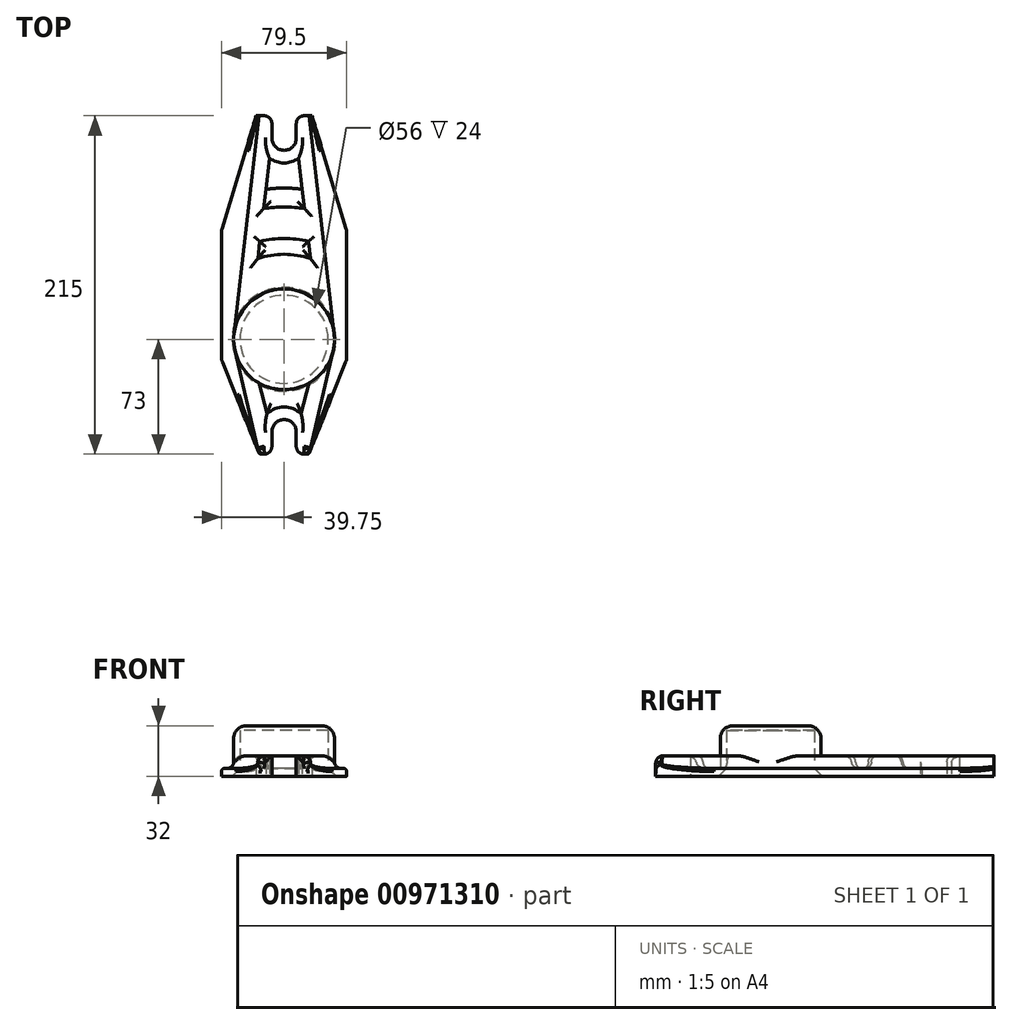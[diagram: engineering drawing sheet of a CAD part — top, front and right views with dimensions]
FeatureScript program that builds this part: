
annotation { "Feature Type Name" : "Feature", "Feature Type Description" : "" }
export const myFeature = defineFeature(function(context is Context, id is Id, definition is map)
    precondition{}
    {
        {
            var Q0;
            Q0=qCreatedBy(makeId("Top.planeOp"),FACE);
            var sketch = newSketch(context, id + "F0", { "sketchPlane" : qUnion([Q0])});
            skCircle(sketch, "E0", {"center": v(0, 0) * mm, "radius": 32 * mm});
            skLineSegment(sketch, "E1.bottom", {"start": v(-17.75, 142) * mm, "end": v(-7.75, 142) * mm});
            skLineSegment(sketch, "E1.top", {"start": v(-15.75, -73) * mm, "end": v(-7.75, -73) * mm});
            skLineSegment(sketch, "E1.left", {"start": v(-39.75, 69) * mm, "end": v(-39.75, -13) * mm});
            skLineSegment(sketch, "E1.right", {"start": v(39.75, 69) * mm, "end": v(39.75, -13) * mm});
            skLineSegment(sketch, "E2", {"start": v(0, 91.94) * mm, "end": v(0, -69.03) * mm, "construction": true});
            skLineSegment(sketch, "E3", {"start": v(-17.75, 142) * mm, "end": v(-39.75, 69) * mm});
            skLineSegment(sketch, "E4", {"start": v(-15.75, -73) * mm, "end": v(-39.75, -13) * mm});
            skArc(sketch, "E5", {"start": v(-7.75, 127.75) * mm, "mid": v(0, 120) * mm, "end": v(7.75, 127.75) * mm});
            skArc(sketch, "E6", {"start": v(7.75, -58.75) * mm, "mid": v(0, -51) * mm, "end": v(-7.75, -58.75) * mm});
            skLineSegment(sketch, "E7.MirrorCS", {"start": v(17.75, 142) * mm, "end": v(39.75, 69) * mm});
            skLineSegment(sketch, "E8.MirrorCS", {"start": v(15.75, -73) * mm, "end": v(39.75, -13) * mm});
            skCircle(sketch, "E9", {"center": v(0, 0) * mm, "radius": 22.5 * mm});
            skLineSegment(sketch, "E10.left", {"start": v(-7.75, 142) * mm, "end": v(-7.75, 127.75) * mm});
            skLineSegment(sketch, "E10.right", {"start": v(7.75, 142) * mm, "end": v(7.75, 127.75) * mm});
            skLineSegment(sketch, "E11.left", {"start": v(-7.75, -58.75) * mm, "end": v(-7.75, -73) * mm});
            skLineSegment(sketch, "E11.right", {"start": v(7.75, -58.75) * mm, "end": v(7.75, -73) * mm});
            skLineSegment(sketch, "E12.0", {"start": v(15.75, 142) * mm, "end": v(15.75, 127.75) * mm});
            skArc(sketch, "E12.1", {"start": v(-15.75, 127.75) * mm, "mid": v(0, 112) * mm, "end": v(15.75, 127.75) * mm});
            skLineSegment(sketch, "E12.2", {"start": v(-15.75, 142) * mm, "end": v(-15.75, 127.75) * mm});
            skLineSegment(sketch, "E13.0", {"start": v(-15.75, -58.75) * mm, "end": v(-15.75, -73) * mm});
            skArc(sketch, "E13.1", {"start": v(15.75, -58.75) * mm, "mid": v(0, -43) * mm, "end": v(-15.75, -58.75) * mm});
            skLineSegment(sketch, "E13.2", {"start": v(15.75, -58.75) * mm, "end": v(15.75, -73) * mm});
            skLineSegment(sketch, "E14.trimOffspring", {"start": v(7.75, 142) * mm, "end": v(17.75, 142) * mm});
            skLineSegment(sketch, "E15.trimOffspring", {"start": v(7.75, -73) * mm, "end": v(15.75, -73) * mm});
            skCircle(sketch, "E16", {"center": v(0, 0) * mm, "radius": 28 * mm});
            skLineSegment(sketch, "E17", {"start": v(-31.79, 3.69) * mm, "end": v(-15.75, 142) * mm});
            skLineSegment(sketch, "E18", {"start": v(31.79, 3.69) * mm, "end": v(15.75, 142) * mm});
            skLineSegment(sketch, "E19", {"start": v(7.75, 127.75) * mm, "end": v(22.65, 0) * mm});
            skLineSegment(sketch, "E20", {"start": v(-7.75, 127.75) * mm, "end": v(-22.35, 2.6) * mm});
            skLineSegment(sketch, "E21", {"start": v(31.15, -7.3) * mm, "end": v(15.75, -73) * mm});
            skLineSegment(sketch, "E22", {"start": v(-31.15, -7.3) * mm, "end": v(-15.75, -73) * mm});
            skLineSegment(sketch, "E23", {"start": v(-21.75, -5.75) * mm, "end": v(-7.75, -58.75) * mm});
            skLineSegment(sketch, "E24", {"start": v(21.75, -5.75) * mm, "end": v(7.75, -58.75) * mm});
            skArc(sketch, "E25", {"start": v(-16.66, 51.37) * mm, "mid": v(0, 54) * mm, "end": v(16.66, 51.37) * mm});
            skArc(sketch, "E26", {"start": v(-15.4, 62.12) * mm, "mid": v(0, 64) * mm, "end": v(15.4, 62.12) * mm});
            skArc(sketch, "E27", {"start": v(-12.97, 83) * mm, "mid": v(0, 84) * mm, "end": v(12.97, 83) * mm});
            skArc(sketch, "E28", {"start": v(-11.53, 95.3) * mm, "mid": v(0, 96) * mm, "end": v(11.53, 95.3) * mm});
            skSolve(sketch);
        }
        {
            var Q0;
            Q0 = qSketchRegion(id + "F0", true);
            var Q1;
            {var subQ0=sQuery(id+"F0.wireOp",EDGE,"E19");var subQ1=sQuery(id+"F0.wireOp",EDGE,"E0");var subQ2=makeQuery(id+"F0.imprint","INTERSECT",VERTEX,{"derivedFrom":[subQ1,subQ0]});Q1=makeQuery(id+"F0.imprint","IMPRINT",FACE,{"disambiguationData":[TD([[makeQuery(id+"F0.imprint","IMPRINT",EDGE,{"disambiguationData":[TD([[subQ2,-1.0]])],"derivedFrom":subQ1}),-1.0]])]});}
            var Q2;
            {var subQ0=sQuery(id+"F0.wireOp",EDGE,"E23");var subQ1=sQuery(id+"F0.wireOp",EDGE,"E0");var subQ2=makeQuery(id+"F0.imprint","INTERSECT",VERTEX,{"derivedFrom":[subQ1,subQ0]});Q2=makeQuery(id+"F0.imprint","IMPRINT",FACE,{"disambiguationData":[TD([[makeQuery(id+"F0.imprint","IMPRINT",EDGE,{"disambiguationData":[TD([[subQ2,-1.0]])],"derivedFrom":subQ1}),-1.0]])]});}
            var Q3;
            {var subQ5=sQuery(id+"F0.wireOp",EDGE,"E26");Q3=makeQuery(id+"F0.imprint","IMPRINT",FACE,{"disambiguationData":[TD([[makeQuery(id+"F0.imprint","IMPRINT",EDGE,{"derivedFrom":subQ5}),1.0]])]});}
            var Q4;
            {var subQ0=sQuery(id+"F0.wireOp",EDGE,"E25");Q4=makeQuery(id+"F0.imprint","IMPRINT",FACE,{"disambiguationData":[TD([[makeQuery(id+"F0.imprint","IMPRINT",EDGE,{"derivedFrom":subQ0}),1.0]])]});}
            var Q5;
            {var subQ0=sQuery(id+"F0.wireOp",EDGE,"E27");Q5=makeQuery(id+"F0.imprint","IMPRINT",FACE,{"disambiguationData":[TD([[makeQuery(id+"F0.imprint","IMPRINT",EDGE,{"derivedFrom":subQ0}),1.0]])]});}
            var Q6;
            {var subQ5=sQuery(id+"F0.wireOp",EDGE,"E28");Q6=makeQuery(id+"F0.imprint","IMPRINT",FACE,{"disambiguationData":[TD([[makeQuery(id+"F0.imprint","IMPRINT",EDGE,{"derivedFrom":subQ5}),1.0]])]});}
            extrude(context, id + "F1", {"entities" : qUnion([Q0, Q1, Q2, Q3, Q4, Q5, Q6]), "depth" : 5 * mm, "offsetDistance" : 25 * mm});
        }
        {
            var Q0;
            Q0=makeQuery(id+"F0.imprint","IMPRINT",FACE,{"disambiguationData":[TD([[makeQuery(id+"F0.imprint","IMPRINT",EDGE,{"derivedFrom":sQuery(id+"F0.wireOp",EDGE,"E6")}),-1.0]])]});
            var Q1;
            Q1=makeQuery(id+"F0.imprint","IMPRINT",FACE,{"disambiguationData":[TD([[makeQuery(id+"F0.imprint","IMPRINT",EDGE,{"derivedFrom":sQuery(id+"F0.wireOp",EDGE,"E5")}),-1.0]])]});
            var Q2;
            {var subQ1=sQuery(id+"F0.wireOp",EDGE,"E10.right");Q2=makeQuery(id+"F0.imprint","IMPRINT",FACE,{"disambiguationData":[TD([[makeQuery(id+"F0.imprint","IMPRINT",EDGE,{"derivedFrom":subQ1}),1.0]])]});}
            var Q3;
            {var subQ4=sQuery(id+"F0.wireOp",EDGE,"E10.left");Q3=makeQuery(id+"F0.imprint","IMPRINT",FACE,{"disambiguationData":[TD([[makeQuery(id+"F0.imprint","IMPRINT",EDGE,{"derivedFrom":subQ4}),-1.0]])]});}
            var Q4;
            Q4=makeQuery(id+"F0.imprint","IMPRINT",FACE,{"disambiguationData":[TD([[makeQuery(id+"F0.imprint","IMPRINT",EDGE,{"derivedFrom":sQuery(id+"F0.wireOp",EDGE,"E1.top")}),1.0]])]});
            var Q5;
            {var subQ4=sQuery(id+"F0.wireOp",EDGE,"E11.right");Q5=makeQuery(id+"F0.imprint","IMPRINT",FACE,{"disambiguationData":[TD([[makeQuery(id+"F0.imprint","IMPRINT",EDGE,{"derivedFrom":subQ4}),1.0]])]});}
            extrude(context, id + "F2", {"entities" : qUnion([Q0, Q1, Q2, Q3, Q4, Q5]), "operationType" : NewBodyOperationType.ADD, "depth" : 13 * mm, "offsetDistance" : 25 * mm});
        }
        {
            var Q0;
            Q0=makeQuery(id+"F0.imprint","IMPRINT",FACE,{"disambiguationData":[TD([[makeQuery(id+"F0.imprint","IMPRINT",EDGE,{"derivedFrom":sQuery(id+"F0.wireOp",EDGE,"E0")}),1.0]])]});
            var Q1;
            {var subQ0=sQuery(id+"F0.wireOp",EDGE,"E19");var subQ1=sQuery(id+"F0.wireOp",EDGE,"E0");var subQ2=makeQuery(id+"F0.imprint","INTERSECT",VERTEX,{"derivedFrom":[subQ1,subQ0]});Q1=makeQuery(id+"F0.imprint","IMPRINT",FACE,{"disambiguationData":[TD([[makeQuery(id+"F0.imprint","IMPRINT",EDGE,{"disambiguationData":[TD([[subQ2,-1.0]])],"derivedFrom":subQ1}),1.0]])]});}
            var Q2;
            {var subQ0=sQuery(id+"F0.wireOp",EDGE,"E23");var subQ1=sQuery(id+"F0.wireOp",EDGE,"E0");var subQ2=makeQuery(id+"F0.imprint","INTERSECT",VERTEX,{"derivedFrom":[subQ1,subQ0]});Q2=makeQuery(id+"F0.imprint","IMPRINT",FACE,{"disambiguationData":[TD([[makeQuery(id+"F0.imprint","IMPRINT",EDGE,{"disambiguationData":[TD([[subQ2,-1.0]])],"derivedFrom":subQ1}),1.0]])]});}
            extrude(context, id + "F3", {"entities" : qUnion([Q0, Q1, Q2]), "operationType" : NewBodyOperationType.ADD, "depth" : 29 * mm, "offsetDistance" : 25 * mm});
        }
        {
            var Q0;
            Q0=makeQuery(id+"F0.imprint","IMPRINT",FACE,{"disambiguationData":[TD([[makeQuery(id+"F0.imprint","IMPRINT",EDGE,{"derivedFrom":sQuery(id+"F0.wireOp",EDGE,"E0")}),1.0]])]});
            var Q1;
            Q1=makeQuery(id+"F0.imprint","IMPRINT",FACE,{"disambiguationData":[TD([[makeQuery(id+"F0.imprint","IMPRINT",EDGE,{"derivedFrom":sQuery(id+"F0.wireOp",EDGE,"E9")}),-1.0]])]});
            var Q2;
            Q2=makeQuery(id+"F0.imprint","IMPRINT",FACE,{"disambiguationData":[TD([[makeQuery(id+"F0.imprint","IMPRINT",EDGE,{"derivedFrom":sQuery(id+"F0.wireOp",EDGE,"E9")}),1.0]])]});
            var Q3;
            {var subQ0=sQuery(id+"F0.wireOp",EDGE,"E19");var subQ1=sQuery(id+"F0.wireOp",EDGE,"E0");var subQ2=makeQuery(id+"F0.imprint","INTERSECT",VERTEX,{"derivedFrom":[subQ1,subQ0]});Q3=makeQuery(id+"F0.imprint","IMPRINT",FACE,{"disambiguationData":[TD([[makeQuery(id+"F0.imprint","IMPRINT",EDGE,{"disambiguationData":[TD([[subQ2,-1.0]])],"derivedFrom":subQ1}),1.0]])]});}
            var Q4;
            {var subQ0=sQuery(id+"F0.wireOp",EDGE,"E23");var subQ1=sQuery(id+"F0.wireOp",EDGE,"E0");var subQ2=makeQuery(id+"F0.imprint","INTERSECT",VERTEX,{"derivedFrom":[subQ1,subQ0]});Q4=makeQuery(id+"F0.imprint","IMPRINT",FACE,{"disambiguationData":[TD([[makeQuery(id+"F0.imprint","IMPRINT",EDGE,{"disambiguationData":[TD([[subQ2,-1.0]])],"derivedFrom":subQ1}),1.0]])]});}
            extrude(context, id + "F4", {"entities" : qUnion([Q0, Q1, Q2, Q3, Q4]), "operationType" : NewBodyOperationType.ADD, "depth" : 32 * mm, "offsetDistance" : 25 * mm, "hasSecondDirection" : true, "secondDirectionOppositeDirection" : false, "secondDirectionDepth" : 29 * mm});
        }
        {
            var Q0;
            {var subQ1=sQuery(id+"F0.wireOp",EDGE,"E12.0");Q0=makeQuery(id+"F0.imprint","IMPRINT",FACE,{"disambiguationData":[TD([[makeQuery(id+"F0.imprint","IMPRINT",EDGE,{"derivedFrom":subQ1}),1.0]])]});}
            var Q1;
            {var subQ1=sQuery(id+"F0.wireOp",EDGE,"E12.2");Q1=makeQuery(id+"F0.imprint","IMPRINT",FACE,{"disambiguationData":[TD([[makeQuery(id+"F0.imprint","IMPRINT",EDGE,{"derivedFrom":subQ1}),-1.0]])]});}
            var Q2;
            {var subQ2=sQuery(id+"F0.wireOp",EDGE,"E13.0");Q2=makeQuery(id+"F0.imprint","IMPRINT",FACE,{"disambiguationData":[TD([[makeQuery(id+"F0.imprint","IMPRINT",EDGE,{"derivedFrom":subQ2}),-1.0]])]});}
            var Q3;
            {var subQ1=sQuery(id+"F0.wireOp",EDGE,"E13.2");Q3=makeQuery(id+"F0.imprint","IMPRINT",FACE,{"disambiguationData":[TD([[makeQuery(id+"F0.imprint","IMPRINT",EDGE,{"derivedFrom":subQ1}),1.0]])]});}
            var Q4;
            {var subQ0=sQuery(id+"F0.wireOp",EDGE,"E25");Q4=makeQuery(id+"F0.imprint","IMPRINT",FACE,{"disambiguationData":[TD([[makeQuery(id+"F0.imprint","IMPRINT",EDGE,{"derivedFrom":subQ0}),1.0]])]});}
            var Q5;
            {var subQ0=sQuery(id+"F0.wireOp",EDGE,"E27");Q5=makeQuery(id+"F0.imprint","IMPRINT",FACE,{"disambiguationData":[TD([[makeQuery(id+"F0.imprint","IMPRINT",EDGE,{"derivedFrom":subQ0}),1.0]])]});}
            extrude(context, id + "F5", {"entities" : qUnion([Q0, Q1, Q2, Q3, Q4, Q5]), "operationType" : NewBodyOperationType.ADD, "depth" : 13 * mm, "offsetDistance" : 25 * mm});
        }
        {
            var Q0;
            Q0=makeQuery(id+"F4.opExtrude","CAP_EDGE",EDGE,{"disambiguationData":[OSD([sQuery(id+"F0.wireOp",EDGE,"E0")])],"isStart":false});
            var Q1;
            Q1=makeQuery(id+"F1.opExtrude","SWEPT_EDGE",EDGE,{"disambiguationData":[OSD([sQuery(id+"F0.wireOp",EDGE,"E1.right"),sQuery(id+"F0.wireOp",EDGE,"E8.MirrorCS")])]});
            var Q2;
            Q2=makeQuery(id+"F1.opExtrude","SWEPT_EDGE",EDGE,{"disambiguationData":[OSD([sQuery(id+"F0.wireOp",EDGE,"E1.right"),sQuery(id+"F0.wireOp",EDGE,"E7.MirrorCS")])]});
            var Q3;
            Q3=makeQuery(id+"F1.opExtrude","SWEPT_EDGE",EDGE,{"disambiguationData":[OSD([sQuery(id+"F0.wireOp",EDGE,"E1.left"),sQuery(id+"F0.wireOp",EDGE,"E4")])]});
            var Q4;
            Q4=makeQuery(id+"F1.opExtrude","SWEPT_EDGE",EDGE,{"disambiguationData":[OSD([sQuery(id+"F0.wireOp",EDGE,"E1.left"),sQuery(id+"F0.wireOp",EDGE,"E3")])]});
            fillet(context, id + "F6", {"entities" : qUnion([Q0, Q1, Q2, Q3, Q4]), "radius" : 8 * mm, "allowEdgeOverflow" : false});
        }
        {
            var Q0;
            Q0=makeQuery(id+"F3.opExtrude","CAP_EDGE",EDGE,{"disambiguationData":[OSD([sQuery(id+"F0.wireOp",EDGE,"E16")])],"isStart":true});
            var Q1;
            Q1=makeQuery(id+"F3.opExtrude","CAP_EDGE",EDGE,{"disambiguationData":[OSD([sQuery(id+"F0.wireOp",EDGE,"E16")])],"isStart":false});
            chamfer(context, id + "F7", {"entities" : qUnion([Q0, Q1]), "width" : 5 * mm, "tangentPropagation" : true});
        }
        {
            var Q0;
            {var subQ0=sQuery(id+"F0.wireOp",EDGE,"E11.left");var subQ1=sQuery(id+"F0.wireOp",EDGE,"E1.top");Q0=makeQuery(id+"F2.boolean.opBoolean","MERGE",EDGE,{"derivedFrom":[makeQuery(id+"F1.opExtrude","SWEPT_EDGE",EDGE,{"disambiguationData":[OSD([subQ1,subQ0])]}),makeQuery(id+"F2.opExtrude","SWEPT_EDGE",EDGE,{"disambiguationData":[OSD([subQ1,subQ0])]})]});}
            var Q1;
            {var subQ0=sQuery(id+"F0.wireOp",EDGE,"E15.trimOffspring");var subQ1=sQuery(id+"F0.wireOp",EDGE,"E11.right");Q1=makeQuery(id+"F2.boolean.opBoolean","MERGE",EDGE,{"derivedFrom":[makeQuery(id+"F1.opExtrude","SWEPT_EDGE",EDGE,{"disambiguationData":[OSD([subQ1,subQ0])]}),makeQuery(id+"F2.opExtrude","SWEPT_EDGE",EDGE,{"disambiguationData":[OSD([subQ1,subQ0])]})]});}
            var Q2;
            {var subQ0=sQuery(id+"F0.wireOp",EDGE,"E10.left");var subQ1=sQuery(id+"F0.wireOp",EDGE,"E1.bottom");Q2=makeQuery(id+"F2.boolean.opBoolean","MERGE",EDGE,{"derivedFrom":[makeQuery(id+"F1.opExtrude","SWEPT_EDGE",EDGE,{"disambiguationData":[OSD([subQ1,subQ0])]}),makeQuery(id+"F2.opExtrude","SWEPT_EDGE",EDGE,{"disambiguationData":[OSD([subQ1,subQ0])]})]});}
            var Q3;
            {var subQ0=sQuery(id+"F0.wireOp",EDGE,"E14.trimOffspring");var subQ1=sQuery(id+"F0.wireOp",EDGE,"E10.right");Q3=makeQuery(id+"F2.boolean.opBoolean","MERGE",EDGE,{"derivedFrom":[makeQuery(id+"F1.opExtrude","SWEPT_EDGE",EDGE,{"disambiguationData":[OSD([subQ1,subQ0])]}),makeQuery(id+"F2.opExtrude","SWEPT_EDGE",EDGE,{"disambiguationData":[OSD([subQ1,subQ0])]})]});}
            fillet(context, id + "F8", {"entities" : qUnion([Q0, Q1, Q2, Q3]), "radius" : 5 * mm, "tangentPropagation" : true, "allowEdgeOverflow" : false});
        }
        {
            var Q0;
            Q0=makeQuery(id+"F5.boolean.opBoolean","INTERSECT",EDGE,{"derivedFrom":[makeQuery(id+"F1.opExtrude","CAP_FACE",FACE,{"disambiguationData":[OSD([sQuery(id+"F0.wireOp",EDGE,"E0"),sQuery(id+"F0.wireOp",EDGE,"E1.bottom"),sQuery(id+"F0.wireOp",EDGE,"E1.top"),sQuery(id+"F0.wireOp",EDGE,"E1.left"),sQuery(id+"F0.wireOp",EDGE,"E1.right"),sQuery(id+"F0.wireOp",EDGE,"E3"),sQuery(id+"F0.wireOp",EDGE,"E4"),sQuery(id+"F0.wireOp",EDGE,"E5"),sQuery(id+"F0.wireOp",EDGE,"E6"),sQuery(id+"F0.wireOp",EDGE,"E7.MirrorCS"),sQuery(id+"F0.wireOp",EDGE,"E8.MirrorCS"),sQuery(id+"F0.wireOp",EDGE,"E10.left"),sQuery(id+"F0.wireOp",EDGE,"E10.right"),sQuery(id+"F0.wireOp",EDGE,"E11.left"),sQuery(id+"F0.wireOp",EDGE,"E11.right"),sQuery(id+"F0.wireOp",EDGE,"E14.trimOffspring"),sQuery(id+"F0.wireOp",EDGE,"E15.trimOffspring")])],"isStart":false}),makeQuery(id+"F5.opExtrude","SWEPT_FACE",FACE,{"disambiguationData":[OSD([sQuery(id+"F0.wireOp",EDGE,"E20")])]})]});
            var Q1;
            {var subQ0=sQuery(id+"F0.wireOp",EDGE,"E0");Q1=makeQuery(id+"F5.boolean.opBoolean","SPLIT",EDGE,{"disambiguationData":[TD([makeQuery(id+"F5.opExtrude","SWEPT_FACE",FACE,{"disambiguationData":[OSD([sQuery(id+"F0.wireOp",EDGE,"E19")])]})])],"derivedFrom":makeQuery(id+"F1.opExtrude","CAP_EDGE",EDGE,{"disambiguationData":[OSD([subQ0])],"isStart":false})});}
            var Q2;
            Q2=makeQuery(id+"F5.opExtrude","CAP_EDGE",EDGE,{"disambiguationData":[OSD([sQuery(id+"F0.wireOp",EDGE,"E20")])],"isStart":false});
            var Q3;
            Q3=makeQuery(id+"F5.boolean.opBoolean","INTERSECT",EDGE,{"derivedFrom":[makeQuery(id+"F1.opExtrude","CAP_FACE",FACE,{"disambiguationData":[OSD([sQuery(id+"F0.wireOp",EDGE,"E0"),sQuery(id+"F0.wireOp",EDGE,"E1.bottom"),sQuery(id+"F0.wireOp",EDGE,"E1.top"),sQuery(id+"F0.wireOp",EDGE,"E1.left"),sQuery(id+"F0.wireOp",EDGE,"E1.right"),sQuery(id+"F0.wireOp",EDGE,"E3"),sQuery(id+"F0.wireOp",EDGE,"E4"),sQuery(id+"F0.wireOp",EDGE,"E5"),sQuery(id+"F0.wireOp",EDGE,"E6"),sQuery(id+"F0.wireOp",EDGE,"E7.MirrorCS"),sQuery(id+"F0.wireOp",EDGE,"E8.MirrorCS"),sQuery(id+"F0.wireOp",EDGE,"E10.left"),sQuery(id+"F0.wireOp",EDGE,"E10.right"),sQuery(id+"F0.wireOp",EDGE,"E11.left"),sQuery(id+"F0.wireOp",EDGE,"E11.right"),sQuery(id+"F0.wireOp",EDGE,"E14.trimOffspring"),sQuery(id+"F0.wireOp",EDGE,"E15.trimOffspring")])],"isStart":false}),makeQuery(id+"F5.opExtrude","SWEPT_FACE",FACE,{"disambiguationData":[OSD([sQuery(id+"F0.wireOp",EDGE,"E19")])]})]});
            var Q4;
            Q4=makeQuery(id+"F5.opExtrude","CAP_EDGE",EDGE,{"disambiguationData":[OSD([sQuery(id+"F0.wireOp",EDGE,"E19")])],"isStart":false});
            var Q5;
            Q5=makeQuery(id+"F2.boolean.opBoolean","INTERSECT",EDGE,{"derivedFrom":[makeQuery(id+"F1.opExtrude","CAP_FACE",FACE,{"disambiguationData":[OSD([sQuery(id+"F0.wireOp",EDGE,"E0"),sQuery(id+"F0.wireOp",EDGE,"E1.bottom"),sQuery(id+"F0.wireOp",EDGE,"E1.top"),sQuery(id+"F0.wireOp",EDGE,"E1.left"),sQuery(id+"F0.wireOp",EDGE,"E1.right"),sQuery(id+"F0.wireOp",EDGE,"E3"),sQuery(id+"F0.wireOp",EDGE,"E4"),sQuery(id+"F0.wireOp",EDGE,"E5"),sQuery(id+"F0.wireOp",EDGE,"E6"),sQuery(id+"F0.wireOp",EDGE,"E7.MirrorCS"),sQuery(id+"F0.wireOp",EDGE,"E8.MirrorCS"),sQuery(id+"F0.wireOp",EDGE,"E10.left"),sQuery(id+"F0.wireOp",EDGE,"E10.right"),sQuery(id+"F0.wireOp",EDGE,"E11.left"),sQuery(id+"F0.wireOp",EDGE,"E11.right"),sQuery(id+"F0.wireOp",EDGE,"E14.trimOffspring"),sQuery(id+"F0.wireOp",EDGE,"E15.trimOffspring")])],"isStart":false}),makeQuery(id+"F2.opExtrude","SWEPT_FACE",FACE,{"disambiguationData":[OSD([sQuery(id+"F0.wireOp",EDGE,"E12.1")])]})]});
            var Q6;
            Q6=makeQuery(id+"F2.opExtrude","CAP_EDGE",EDGE,{"disambiguationData":[OSD([sQuery(id+"F0.wireOp",EDGE,"E12.1")])],"isStart":false});
            var Q7;
            Q7=makeQuery(id+"F5.opExtrude","CAP_EDGE",EDGE,{"disambiguationData":[OSD([sQuery(id+"F0.wireOp",EDGE,"E18")])],"isStart":false});
            var Q8;
            Q8=makeQuery(id+"F5.opExtrude","CAP_EDGE",EDGE,{"disambiguationData":[OSD([sQuery(id+"F0.wireOp",EDGE,"E17")])],"isStart":false});
            var Q9;
            Q9=makeQuery(id+"F5.opExtrude","CAP_EDGE",EDGE,{"disambiguationData":[OSD([sQuery(id+"F0.wireOp",EDGE,"E22")])],"isStart":false});
            var Q10;
            {var subQ0=sQuery(id+"F0.wireOp",EDGE,"E0");Q10=makeQuery(id+"F5.boolean.opBoolean","SPLIT",EDGE,{"disambiguationData":[TD([makeQuery(id+"F5.opExtrude","SWEPT_FACE",FACE,{"disambiguationData":[OSD([sQuery(id+"F0.wireOp",EDGE,"E23")])]})])],"derivedFrom":makeQuery(id+"F1.opExtrude","CAP_EDGE",EDGE,{"disambiguationData":[OSD([subQ0])],"isStart":false})});}
            var Q11;
            Q11=makeQuery(id+"F5.opExtrude","CAP_EDGE",EDGE,{"disambiguationData":[OSD([sQuery(id+"F0.wireOp",EDGE,"E23")])],"isStart":false});
            var Q12;
            Q12=makeQuery(id+"F5.opExtrude","CAP_EDGE",EDGE,{"disambiguationData":[OSD([sQuery(id+"F0.wireOp",EDGE,"E24")])],"isStart":false});
            var Q13;
            Q13=makeQuery(id+"F2.opExtrude","CAP_EDGE",EDGE,{"disambiguationData":[OSD([sQuery(id+"F0.wireOp",EDGE,"E13.1")])],"isStart":false});
            var Q14;
            Q14=makeQuery(id+"F5.boolean.opBoolean","INTERSECT",EDGE,{"derivedFrom":[makeQuery(id+"F1.opExtrude","CAP_FACE",FACE,{"disambiguationData":[OSD([sQuery(id+"F0.wireOp",EDGE,"E0"),sQuery(id+"F0.wireOp",EDGE,"E1.bottom"),sQuery(id+"F0.wireOp",EDGE,"E1.top"),sQuery(id+"F0.wireOp",EDGE,"E1.left"),sQuery(id+"F0.wireOp",EDGE,"E1.right"),sQuery(id+"F0.wireOp",EDGE,"E3"),sQuery(id+"F0.wireOp",EDGE,"E4"),sQuery(id+"F0.wireOp",EDGE,"E5"),sQuery(id+"F0.wireOp",EDGE,"E6"),sQuery(id+"F0.wireOp",EDGE,"E7.MirrorCS"),sQuery(id+"F0.wireOp",EDGE,"E8.MirrorCS"),sQuery(id+"F0.wireOp",EDGE,"E10.left"),sQuery(id+"F0.wireOp",EDGE,"E10.right"),sQuery(id+"F0.wireOp",EDGE,"E11.left"),sQuery(id+"F0.wireOp",EDGE,"E11.right"),sQuery(id+"F0.wireOp",EDGE,"E14.trimOffspring"),sQuery(id+"F0.wireOp",EDGE,"E15.trimOffspring")])],"isStart":false}),makeQuery(id+"F5.opExtrude","SWEPT_FACE",FACE,{"disambiguationData":[OSD([sQuery(id+"F0.wireOp",EDGE,"E24")])]})]});
            var Q15;
            Q15=makeQuery(id+"F2.boolean.opBoolean","INTERSECT",EDGE,{"derivedFrom":[makeQuery(id+"F1.opExtrude","CAP_FACE",FACE,{"disambiguationData":[OSD([sQuery(id+"F0.wireOp",EDGE,"E0"),sQuery(id+"F0.wireOp",EDGE,"E1.bottom"),sQuery(id+"F0.wireOp",EDGE,"E1.top"),sQuery(id+"F0.wireOp",EDGE,"E1.left"),sQuery(id+"F0.wireOp",EDGE,"E1.right"),sQuery(id+"F0.wireOp",EDGE,"E3"),sQuery(id+"F0.wireOp",EDGE,"E4"),sQuery(id+"F0.wireOp",EDGE,"E5"),sQuery(id+"F0.wireOp",EDGE,"E6"),sQuery(id+"F0.wireOp",EDGE,"E7.MirrorCS"),sQuery(id+"F0.wireOp",EDGE,"E8.MirrorCS"),sQuery(id+"F0.wireOp",EDGE,"E10.left"),sQuery(id+"F0.wireOp",EDGE,"E10.right"),sQuery(id+"F0.wireOp",EDGE,"E11.left"),sQuery(id+"F0.wireOp",EDGE,"E11.right"),sQuery(id+"F0.wireOp",EDGE,"E14.trimOffspring"),sQuery(id+"F0.wireOp",EDGE,"E15.trimOffspring")])],"isStart":false}),makeQuery(id+"F2.opExtrude","SWEPT_FACE",FACE,{"disambiguationData":[OSD([sQuery(id+"F0.wireOp",EDGE,"E13.1")])]})]});
            var Q16;
            Q16=makeQuery(id+"F5.boolean.opBoolean","INTERSECT",EDGE,{"derivedFrom":[makeQuery(id+"F1.opExtrude","CAP_FACE",FACE,{"disambiguationData":[OSD([sQuery(id+"F0.wireOp",EDGE,"E0"),sQuery(id+"F0.wireOp",EDGE,"E1.bottom"),sQuery(id+"F0.wireOp",EDGE,"E1.top"),sQuery(id+"F0.wireOp",EDGE,"E1.left"),sQuery(id+"F0.wireOp",EDGE,"E1.right"),sQuery(id+"F0.wireOp",EDGE,"E3"),sQuery(id+"F0.wireOp",EDGE,"E4"),sQuery(id+"F0.wireOp",EDGE,"E5"),sQuery(id+"F0.wireOp",EDGE,"E6"),sQuery(id+"F0.wireOp",EDGE,"E7.MirrorCS"),sQuery(id+"F0.wireOp",EDGE,"E8.MirrorCS"),sQuery(id+"F0.wireOp",EDGE,"E10.left"),sQuery(id+"F0.wireOp",EDGE,"E10.right"),sQuery(id+"F0.wireOp",EDGE,"E11.left"),sQuery(id+"F0.wireOp",EDGE,"E11.right"),sQuery(id+"F0.wireOp",EDGE,"E14.trimOffspring"),sQuery(id+"F0.wireOp",EDGE,"E15.trimOffspring")])],"isStart":false}),makeQuery(id+"F5.opExtrude","SWEPT_FACE",FACE,{"disambiguationData":[OSD([sQuery(id+"F0.wireOp",EDGE,"E23")])]})]});
            var Q17;
            Q17=makeQuery(id+"F5.opExtrude","CAP_EDGE",EDGE,{"disambiguationData":[OSD([sQuery(id+"F0.wireOp",EDGE,"E21")])],"isStart":false});
            var Q18;
            {var subQ0=sQuery(id+"F0.wireOp",EDGE,"E0");Q18=makeQuery(id+"F5.boolean.opBoolean","SPLIT",EDGE,{"disambiguationData":[TD([makeQuery(id+"F5.opExtrude","SWEPT_FACE",FACE,{"disambiguationData":[OSD([sQuery(id+"F0.wireOp",EDGE,"E17")])]})])],"derivedFrom":makeQuery(id+"F1.opExtrude","CAP_EDGE",EDGE,{"disambiguationData":[OSD([subQ0])],"isStart":false})});}
            var Q19;
            Q19=makeQuery(id+"F5.boolean.opBoolean","INTERSECT",EDGE,{"derivedFrom":[makeQuery(id+"F1.opExtrude","CAP_FACE",FACE,{"disambiguationData":[OSD([sQuery(id+"F0.wireOp",EDGE,"E0"),sQuery(id+"F0.wireOp",EDGE,"E1.bottom"),sQuery(id+"F0.wireOp",EDGE,"E1.top"),sQuery(id+"F0.wireOp",EDGE,"E1.left"),sQuery(id+"F0.wireOp",EDGE,"E1.right"),sQuery(id+"F0.wireOp",EDGE,"E3"),sQuery(id+"F0.wireOp",EDGE,"E4"),sQuery(id+"F0.wireOp",EDGE,"E5"),sQuery(id+"F0.wireOp",EDGE,"E6"),sQuery(id+"F0.wireOp",EDGE,"E7.MirrorCS"),sQuery(id+"F0.wireOp",EDGE,"E8.MirrorCS"),sQuery(id+"F0.wireOp",EDGE,"E10.left"),sQuery(id+"F0.wireOp",EDGE,"E10.right"),sQuery(id+"F0.wireOp",EDGE,"E11.left"),sQuery(id+"F0.wireOp",EDGE,"E11.right"),sQuery(id+"F0.wireOp",EDGE,"E14.trimOffspring"),sQuery(id+"F0.wireOp",EDGE,"E15.trimOffspring")])],"isStart":false}),makeQuery(id+"F5.opExtrude","SWEPT_FACE",FACE,{"disambiguationData":[OSD([sQuery(id+"F0.wireOp",EDGE,"E17")])]})]});
            var Q20;
            {var subQ0=sQuery(id+"F0.wireOp",EDGE,"E0");Q20=makeQuery(id+"F5.boolean.opBoolean","SPLIT",EDGE,{"disambiguationData":[TD([makeQuery(id+"F5.opExtrude","SWEPT_FACE",FACE,{"disambiguationData":[OSD([sQuery(id+"F0.wireOp",EDGE,"E18")])]})])],"derivedFrom":makeQuery(id+"F1.opExtrude","CAP_EDGE",EDGE,{"disambiguationData":[OSD([subQ0])],"isStart":false})});}
            var Q21;
            Q21=makeQuery(id+"F5.boolean.opBoolean","INTERSECT",EDGE,{"derivedFrom":[makeQuery(id+"F1.opExtrude","CAP_FACE",FACE,{"disambiguationData":[OSD([sQuery(id+"F0.wireOp",EDGE,"E0"),sQuery(id+"F0.wireOp",EDGE,"E1.bottom"),sQuery(id+"F0.wireOp",EDGE,"E1.top"),sQuery(id+"F0.wireOp",EDGE,"E1.left"),sQuery(id+"F0.wireOp",EDGE,"E1.right"),sQuery(id+"F0.wireOp",EDGE,"E3"),sQuery(id+"F0.wireOp",EDGE,"E4"),sQuery(id+"F0.wireOp",EDGE,"E5"),sQuery(id+"F0.wireOp",EDGE,"E6"),sQuery(id+"F0.wireOp",EDGE,"E7.MirrorCS"),sQuery(id+"F0.wireOp",EDGE,"E8.MirrorCS"),sQuery(id+"F0.wireOp",EDGE,"E10.left"),sQuery(id+"F0.wireOp",EDGE,"E10.right"),sQuery(id+"F0.wireOp",EDGE,"E11.left"),sQuery(id+"F0.wireOp",EDGE,"E11.right"),sQuery(id+"F0.wireOp",EDGE,"E14.trimOffspring"),sQuery(id+"F0.wireOp",EDGE,"E15.trimOffspring")])],"isStart":false}),makeQuery(id+"F5.opExtrude","SWEPT_FACE",FACE,{"disambiguationData":[OSD([sQuery(id+"F0.wireOp",EDGE,"E18")])]})]});
            var Q22;
            Q22=makeQuery(id+"F5.boolean.opBoolean","INTERSECT",EDGE,{"derivedFrom":[makeQuery(id+"F1.opExtrude","CAP_FACE",FACE,{"disambiguationData":[OSD([sQuery(id+"F0.wireOp",EDGE,"E0"),sQuery(id+"F0.wireOp",EDGE,"E1.bottom"),sQuery(id+"F0.wireOp",EDGE,"E1.top"),sQuery(id+"F0.wireOp",EDGE,"E1.left"),sQuery(id+"F0.wireOp",EDGE,"E1.right"),sQuery(id+"F0.wireOp",EDGE,"E3"),sQuery(id+"F0.wireOp",EDGE,"E4"),sQuery(id+"F0.wireOp",EDGE,"E5"),sQuery(id+"F0.wireOp",EDGE,"E6"),sQuery(id+"F0.wireOp",EDGE,"E7.MirrorCS"),sQuery(id+"F0.wireOp",EDGE,"E8.MirrorCS"),sQuery(id+"F0.wireOp",EDGE,"E10.left"),sQuery(id+"F0.wireOp",EDGE,"E10.right"),sQuery(id+"F0.wireOp",EDGE,"E11.left"),sQuery(id+"F0.wireOp",EDGE,"E11.right"),sQuery(id+"F0.wireOp",EDGE,"E14.trimOffspring"),sQuery(id+"F0.wireOp",EDGE,"E15.trimOffspring")])],"isStart":false}),makeQuery(id+"F5.opExtrude","SWEPT_FACE",FACE,{"disambiguationData":[OSD([sQuery(id+"F0.wireOp",EDGE,"E22")])]})]});
            var Q23;
            Q23=makeQuery(id+"F5.boolean.opBoolean","INTERSECT",EDGE,{"derivedFrom":[makeQuery(id+"F1.opExtrude","CAP_FACE",FACE,{"disambiguationData":[OSD([sQuery(id+"F0.wireOp",EDGE,"E0"),sQuery(id+"F0.wireOp",EDGE,"E1.bottom"),sQuery(id+"F0.wireOp",EDGE,"E1.top"),sQuery(id+"F0.wireOp",EDGE,"E1.left"),sQuery(id+"F0.wireOp",EDGE,"E1.right"),sQuery(id+"F0.wireOp",EDGE,"E3"),sQuery(id+"F0.wireOp",EDGE,"E4"),sQuery(id+"F0.wireOp",EDGE,"E5"),sQuery(id+"F0.wireOp",EDGE,"E6"),sQuery(id+"F0.wireOp",EDGE,"E7.MirrorCS"),sQuery(id+"F0.wireOp",EDGE,"E8.MirrorCS"),sQuery(id+"F0.wireOp",EDGE,"E10.left"),sQuery(id+"F0.wireOp",EDGE,"E10.right"),sQuery(id+"F0.wireOp",EDGE,"E11.left"),sQuery(id+"F0.wireOp",EDGE,"E11.right"),sQuery(id+"F0.wireOp",EDGE,"E14.trimOffspring"),sQuery(id+"F0.wireOp",EDGE,"E15.trimOffspring")])],"isStart":false}),makeQuery(id+"F5.opExtrude","SWEPT_FACE",FACE,{"disambiguationData":[OSD([sQuery(id+"F0.wireOp",EDGE,"E21")])]})]});
            var Q24;
            Q24=makeQuery(id+"F5.boolean.opBoolean","INTERSECT",EDGE,{"derivedFrom":[makeQuery(id+"F1.opExtrude","CAP_FACE",FACE,{"disambiguationData":[OSD([sQuery(id+"F0.wireOp",EDGE,"E0"),sQuery(id+"F0.wireOp",EDGE,"E1.bottom"),sQuery(id+"F0.wireOp",EDGE,"E1.top"),sQuery(id+"F0.wireOp",EDGE,"E1.left"),sQuery(id+"F0.wireOp",EDGE,"E1.right"),sQuery(id+"F0.wireOp",EDGE,"E3"),sQuery(id+"F0.wireOp",EDGE,"E4"),sQuery(id+"F0.wireOp",EDGE,"E5"),sQuery(id+"F0.wireOp",EDGE,"E6"),sQuery(id+"F0.wireOp",EDGE,"E7.MirrorCS"),sQuery(id+"F0.wireOp",EDGE,"E8.MirrorCS"),sQuery(id+"F0.wireOp",EDGE,"E10.left"),sQuery(id+"F0.wireOp",EDGE,"E10.right"),sQuery(id+"F0.wireOp",EDGE,"E11.left"),sQuery(id+"F0.wireOp",EDGE,"E11.right"),sQuery(id+"F0.wireOp",EDGE,"E14.trimOffspring"),sQuery(id+"F0.wireOp",EDGE,"E15.trimOffspring")])],"isStart":false}),makeQuery(id+"F5.opExtrude","SWEPT_FACE",FACE,{"disambiguationData":[OSD([sQuery(id+"F0.wireOp",EDGE,"E25")])]})]});
            var Q25;
            Q25=makeQuery(id+"F5.opExtrude","CAP_EDGE",EDGE,{"disambiguationData":[OSD([sQuery(id+"F0.wireOp",EDGE,"E25")])],"isStart":false});
            var Q26;
            Q26=makeQuery(id+"F5.opExtrude","CAP_EDGE",EDGE,{"disambiguationData":[OSD([sQuery(id+"F0.wireOp",EDGE,"E26")])],"isStart":false});
            var Q27;
            Q27=makeQuery(id+"F5.boolean.opBoolean","INTERSECT",EDGE,{"derivedFrom":[makeQuery(id+"F1.opExtrude","CAP_FACE",FACE,{"disambiguationData":[OSD([sQuery(id+"F0.wireOp",EDGE,"E0"),sQuery(id+"F0.wireOp",EDGE,"E1.bottom"),sQuery(id+"F0.wireOp",EDGE,"E1.top"),sQuery(id+"F0.wireOp",EDGE,"E1.left"),sQuery(id+"F0.wireOp",EDGE,"E1.right"),sQuery(id+"F0.wireOp",EDGE,"E3"),sQuery(id+"F0.wireOp",EDGE,"E4"),sQuery(id+"F0.wireOp",EDGE,"E5"),sQuery(id+"F0.wireOp",EDGE,"E6"),sQuery(id+"F0.wireOp",EDGE,"E7.MirrorCS"),sQuery(id+"F0.wireOp",EDGE,"E8.MirrorCS"),sQuery(id+"F0.wireOp",EDGE,"E10.left"),sQuery(id+"F0.wireOp",EDGE,"E10.right"),sQuery(id+"F0.wireOp",EDGE,"E11.left"),sQuery(id+"F0.wireOp",EDGE,"E11.right"),sQuery(id+"F0.wireOp",EDGE,"E14.trimOffspring"),sQuery(id+"F0.wireOp",EDGE,"E15.trimOffspring")])],"isStart":false}),makeQuery(id+"F5.opExtrude","SWEPT_FACE",FACE,{"disambiguationData":[OSD([sQuery(id+"F0.wireOp",EDGE,"E26")])]})]});
            var Q28;
            Q28=makeQuery(id+"F5.boolean.opBoolean","INTERSECT",EDGE,{"derivedFrom":[makeQuery(id+"F1.opExtrude","CAP_FACE",FACE,{"disambiguationData":[OSD([sQuery(id+"F0.wireOp",EDGE,"E0"),sQuery(id+"F0.wireOp",EDGE,"E1.bottom"),sQuery(id+"F0.wireOp",EDGE,"E1.top"),sQuery(id+"F0.wireOp",EDGE,"E1.left"),sQuery(id+"F0.wireOp",EDGE,"E1.right"),sQuery(id+"F0.wireOp",EDGE,"E3"),sQuery(id+"F0.wireOp",EDGE,"E4"),sQuery(id+"F0.wireOp",EDGE,"E5"),sQuery(id+"F0.wireOp",EDGE,"E6"),sQuery(id+"F0.wireOp",EDGE,"E7.MirrorCS"),sQuery(id+"F0.wireOp",EDGE,"E8.MirrorCS"),sQuery(id+"F0.wireOp",EDGE,"E10.left"),sQuery(id+"F0.wireOp",EDGE,"E10.right"),sQuery(id+"F0.wireOp",EDGE,"E11.left"),sQuery(id+"F0.wireOp",EDGE,"E11.right"),sQuery(id+"F0.wireOp",EDGE,"E14.trimOffspring"),sQuery(id+"F0.wireOp",EDGE,"E15.trimOffspring")])],"isStart":false}),makeQuery(id+"F5.opExtrude","SWEPT_FACE",FACE,{"disambiguationData":[OSD([sQuery(id+"F0.wireOp",EDGE,"E27")])]})]});
            var Q29;
            Q29=makeQuery(id+"F5.opExtrude","CAP_EDGE",EDGE,{"disambiguationData":[OSD([sQuery(id+"F0.wireOp",EDGE,"E27")])],"isStart":false});
            var Q30;
            Q30=makeQuery(id+"F5.boolean.opBoolean","INTERSECT",EDGE,{"derivedFrom":[makeQuery(id+"F1.opExtrude","CAP_FACE",FACE,{"disambiguationData":[OSD([sQuery(id+"F0.wireOp",EDGE,"E0"),sQuery(id+"F0.wireOp",EDGE,"E1.bottom"),sQuery(id+"F0.wireOp",EDGE,"E1.top"),sQuery(id+"F0.wireOp",EDGE,"E1.left"),sQuery(id+"F0.wireOp",EDGE,"E1.right"),sQuery(id+"F0.wireOp",EDGE,"E3"),sQuery(id+"F0.wireOp",EDGE,"E4"),sQuery(id+"F0.wireOp",EDGE,"E5"),sQuery(id+"F0.wireOp",EDGE,"E6"),sQuery(id+"F0.wireOp",EDGE,"E7.MirrorCS"),sQuery(id+"F0.wireOp",EDGE,"E8.MirrorCS"),sQuery(id+"F0.wireOp",EDGE,"E10.left"),sQuery(id+"F0.wireOp",EDGE,"E10.right"),sQuery(id+"F0.wireOp",EDGE,"E11.left"),sQuery(id+"F0.wireOp",EDGE,"E11.right"),sQuery(id+"F0.wireOp",EDGE,"E14.trimOffspring"),sQuery(id+"F0.wireOp",EDGE,"E15.trimOffspring")])],"isStart":false}),makeQuery(id+"F5.opExtrude","SWEPT_FACE",FACE,{"disambiguationData":[OSD([sQuery(id+"F0.wireOp",EDGE,"E28")])]})]});
            var Q31;
            Q31=makeQuery(id+"F5.opExtrude","CAP_EDGE",EDGE,{"disambiguationData":[OSD([sQuery(id+"F0.wireOp",EDGE,"E28")])],"isStart":false});
            fillet(context, id + "F9", {"entities" : qUnion([Q0, Q1, Q2, Q3, Q4, Q5, Q6, Q7, Q8, Q9, Q10, Q11, Q12, Q13, Q14, Q15, Q16, Q17, Q18, Q19, Q20, Q21, Q22, Q23, Q24, Q25, Q26, Q27, Q28, Q29, Q30, Q31]), "radius" : 4 * mm, "allowEdgeOverflow" : false});
        }
        {
            var Q0;
            {var subQ0=sQuery(id+"F0.wireOp",EDGE,"E15.trimOffspring");Q0=makeQuery(id+"F9.opFillet","BLEND_EDGE",EDGE,{"blendedFrom":[makeQuery(id+"F5.opExtrude","CAP_EDGE",EDGE,{"disambiguationData":[OSD([sQuery(id+"F0.wireOp",EDGE,"E21")])],"isStart":false}),makeQuery(id+"F2.boolean.opBoolean","MERGE",FACE,{"derivedFrom":[makeQuery(id+"F1.opExtrude","SWEPT_FACE",FACE,{"disambiguationData":[OSD([subQ0])]}),makeQuery(id+"F2.opExtrude","SWEPT_FACE",FACE,{"disambiguationData":[OSD([subQ0])]})]})],"blendedInto":[makeQuery(id+"F2.boolean.opBoolean","MERGE",FACE,{"derivedFrom":[makeQuery(id+"F1.opExtrude","SWEPT_FACE",FACE,{"disambiguationData":[OSD([subQ0])]}),makeQuery(id+"F2.opExtrude","SWEPT_FACE",FACE,{"disambiguationData":[OSD([subQ0])]})]})]});}
            var Q1;
            {var subQ0=sQuery(id+"F0.wireOp",EDGE,"E1.top");Q1=makeQuery(id+"F9.opFillet","BLEND_EDGE",EDGE,{"blendedFrom":[makeQuery(id+"F5.opExtrude","CAP_EDGE",EDGE,{"disambiguationData":[OSD([sQuery(id+"F0.wireOp",EDGE,"E22")])],"isStart":false}),makeQuery(id+"F2.boolean.opBoolean","MERGE",FACE,{"derivedFrom":[makeQuery(id+"F1.opExtrude","SWEPT_FACE",FACE,{"disambiguationData":[OSD([subQ0])]}),makeQuery(id+"F2.opExtrude","SWEPT_FACE",FACE,{"disambiguationData":[OSD([subQ0])]})]})],"blendedInto":[makeQuery(id+"F2.boolean.opBoolean","MERGE",FACE,{"derivedFrom":[makeQuery(id+"F1.opExtrude","SWEPT_FACE",FACE,{"disambiguationData":[OSD([subQ0])]}),makeQuery(id+"F2.opExtrude","SWEPT_FACE",FACE,{"disambiguationData":[OSD([subQ0])]})]})]});}
            fillet(context, id + "F10", {"entities" : qUnion([Q0, Q1]), "radius" : 5 * mm, "allowEdgeOverflow" : false});
        }
        {
            var Q0;
            Q0=makeQuery(id+"F1.opExtrude","CAP_EDGE",EDGE,{"disambiguationData":[OSD([sQuery(id+"F0.wireOp",EDGE,"E4")])],"isStart":false});
            var Q1;
            Q1=makeQuery(id+"F1.opExtrude","CAP_EDGE",EDGE,{"disambiguationData":[OSD([sQuery(id+"F0.wireOp",EDGE,"E8.MirrorCS")])],"isStart":false});
            fillet(context, id + "F11", {"entities" : qUnion([Q0, Q1]), "radius" : 2 * mm, "tangentPropagation" : true, "allowEdgeOverflow" : false});
        }
    });
